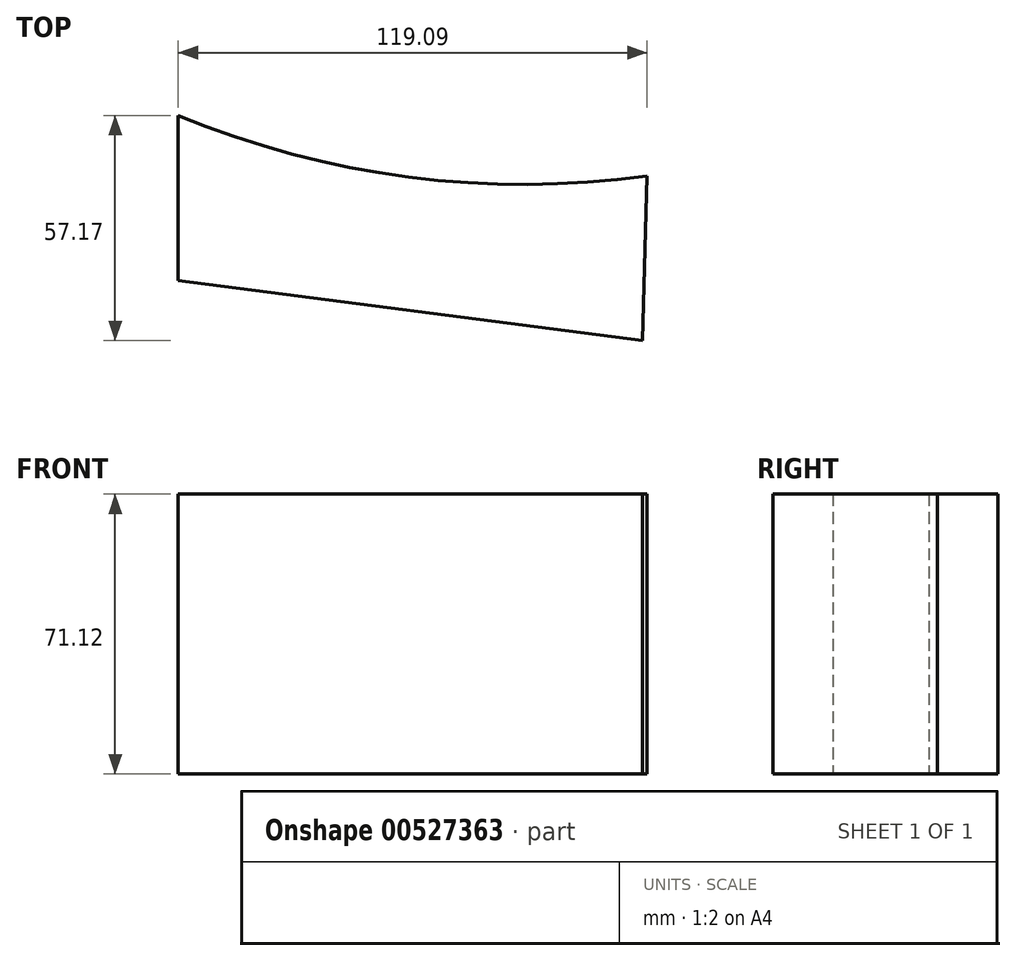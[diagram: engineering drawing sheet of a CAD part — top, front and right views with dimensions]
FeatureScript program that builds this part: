
annotation { "Feature Type Name" : "Feature", "Feature Type Description" : "" }
export const myFeature = defineFeature(function(context is Context, id is Id, definition is map)
    precondition{}
    {
        {
            var Q0;
            Q0=qCreatedBy(makeId("Top.planeOp"),FACE);
            var sketch = newSketch(context, id + "F0", { "sketchPlane" : qUnion([Q0])});
            skCircle(sketch, "E0", {"center": v(0, 0) * mm, "radius": 228.6 * mm});
            skLineSegment(sketch, "E1", {"start": v(31.34, -226.44) * mm, "end": v(-87.75, -211.09) * mm});
            skLineSegment(sketch, "E2", {"start": v(-87.75, -211.09) * mm, "end": v(-87.75, -253.04) * mm});
            skLineSegment(sketch, "E3", {"start": v(-87.75, -253.04) * mm, "end": v(30.21, -268.26) * mm});
            skLineSegment(sketch, "E4", {"start": v(30.21, -268.26) * mm, "end": v(31.34, -226.44) * mm});
            skSolve(sketch);
        }
        {
            var Q0;
            Q0=sQuery(id+"F0.wireOp",EDGE,"E0");
            extrude(context, id + "F1", {"bodyType" : ToolBodyType.SURFACE, "surfaceEntities" : qUnion([Q0]), "depth" : 76.2 * mm, "offsetDistance" : 25.4 * mm});
        }
        {
            var Q0;
            {var subQ3=sQuery(id+"F0.wireOp",EDGE,"E2");Q0=makeQuery(id+"F0.imprint","IMPRINT",FACE,{"disambiguationData":[TD([[makeQuery(id+"F0.imprint","IMPRINT",EDGE,{"derivedFrom":subQ3}),1.0]])]});}
            extrude(context, id + "F2", {"entities" : qUnion([Q0]), "depth" : 71.12 * mm, "offsetDistance" : 25.4 * mm});
        }
    });
